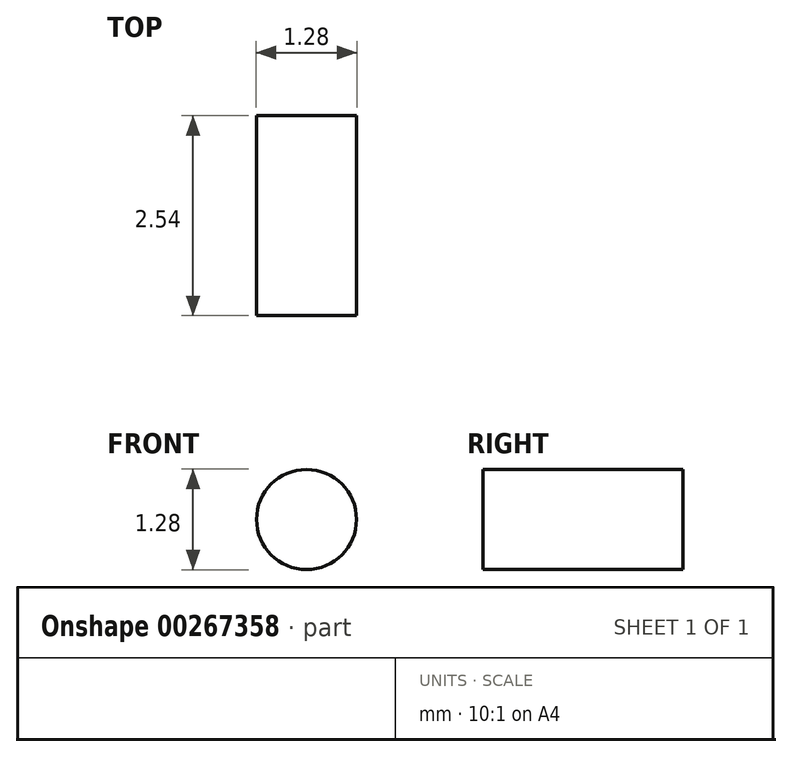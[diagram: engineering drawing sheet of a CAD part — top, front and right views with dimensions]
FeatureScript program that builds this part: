
annotation { "Feature Type Name" : "Feature", "Feature Type Description" : "" }
export const myFeature = defineFeature(function(context is Context, id is Id, definition is map)
    precondition{}
    {
        {
            var Q0;
            Q0=qCreatedBy(makeId("Front.planeOp"),FACE);
            var sketch = newSketch(context, id + "F0", { "sketchPlane" : qUnion([Q0])});
            skCircle(sketch, "E0", {"center": v(0, 0) * mm, "radius": 0.64 * mm});
            skSolve(sketch);
        }
        {
            var Q0;
            Q0 = qSketchRegion(id + "F0", true);
            extrude(context, id + "F1", {"entities" : qUnion([Q0]), "depth" : 2.54 * mm});
        }
    });
